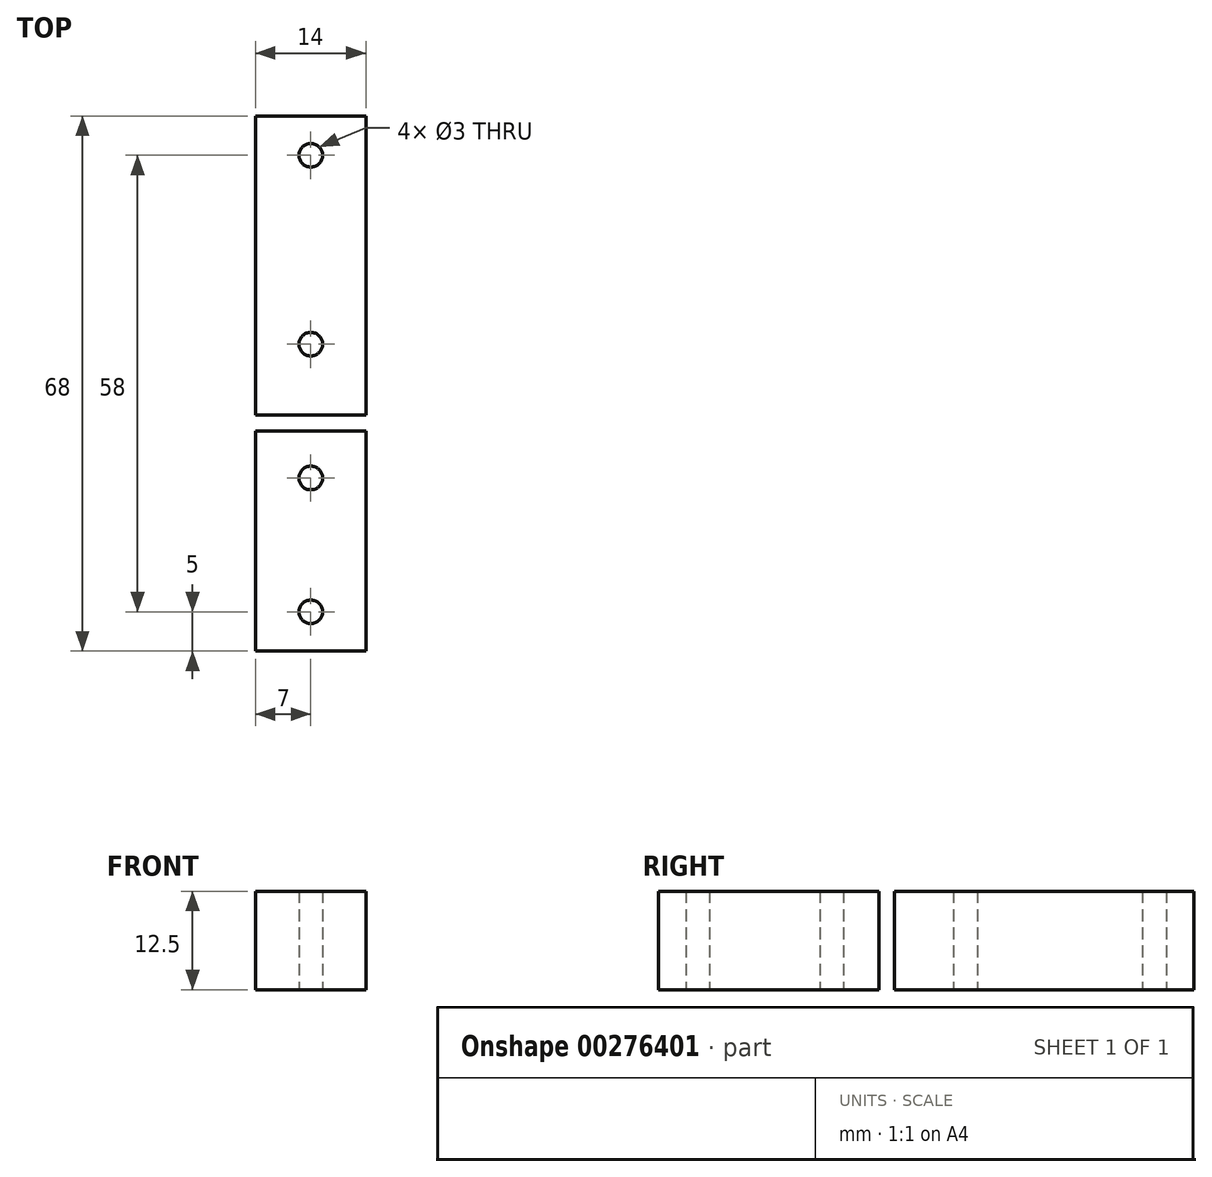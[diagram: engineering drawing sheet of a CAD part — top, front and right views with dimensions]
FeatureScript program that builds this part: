
annotation { "Feature Type Name" : "Feature", "Feature Type Description" : "" }
export const myFeature = defineFeature(function(context is Context, id is Id, definition is map)
    precondition{}
    {
        {
            var Q0;
            Q0=qCreatedBy(makeId("Top.planeOp"),FACE);
            var sketch = newSketch(context, id + "F0", { "sketchPlane" : qUnion([Q0])});
            skLineSegment(sketch, "E0.bottom", {"start": v(0, 0) * mm, "end": v(14, 0) * mm});
            skLineSegment(sketch, "E0.top", {"start": v(0, 68) * mm, "end": v(14, 68) * mm});
            skLineSegment(sketch, "E0.left", {"start": v(0, 0) * mm, "end": v(0, 28) * mm});
            skLineSegment(sketch, "E0.right", {"start": v(14, 0) * mm, "end": v(14, 28) * mm});
            skCircle(sketch, "E1", {"center": v(7, 5) * mm, "radius": 1.5 * mm});
            skPoint(sketch, "E1.centerSnap0", {"position": v(7, 0) * mm});
            skCircle(sketch, "E2", {"center": v(7, 22) * mm, "radius": 1.5 * mm});
            skLineSegment(sketch, "E3.bottom", {"start": v(0, 30) * mm, "end": v(14, 30) * mm});
            skLineSegment(sketch, "E3.top", {"start": v(0, 28) * mm, "end": v(14, 28) * mm});
            skLineSegment(sketch, "E4.trimOffspring", {"start": v(0, 30) * mm, "end": v(0, 68) * mm});
            skCircle(sketch, "E5", {"center": v(7, 39) * mm, "radius": 1.5 * mm});
            skLineSegment(sketch, "E6.trimOffspring", {"start": v(14, 30) * mm, "end": v(14, 68) * mm});
            skCircle(sketch, "E7", {"center": v(7, 63) * mm, "radius": 1.5 * mm});
            skSolve(sketch);
        }
        {
            var Q0;
            Q0 = qSketchRegion(id + "F0", true);
            extrude(context, id + "F1", {"entities" : qUnion([Q0]), "depth" : 12.5 * mm});
        }
    });
